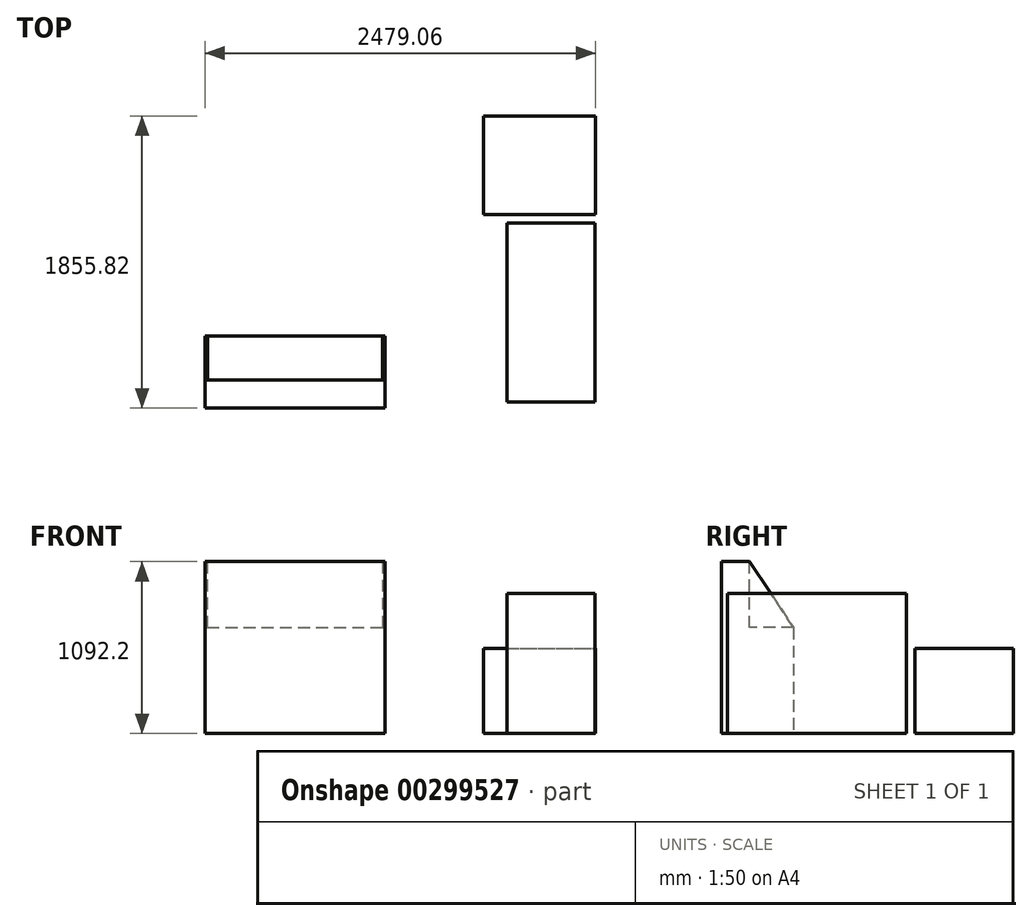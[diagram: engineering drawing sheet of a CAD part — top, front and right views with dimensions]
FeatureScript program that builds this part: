
annotation { "Feature Type Name" : "Feature", "Feature Type Description" : "" }
export const myFeature = defineFeature(function(context is Context, id is Id, definition is map)
    precondition{}
    {
        {
            var Q0;
            Q0=qCreatedBy(makeId("Top.planeOp"),FACE);
            var sketch = newSketch(context, id + "F0", { "sketchPlane" : qUnion([Q0])});
            skLineSegment(sketch, "E0.bottom", {"start": v(0, 2438.4) * mm, "end": v(2514.6, 2438.4) * mm});
            skLineSegment(sketch, "E0.top", {"start": v(0, 0) * mm, "end": v(2514.6, 0) * mm});
            skLineSegment(sketch, "E0.right", {"start": v(2514.6, 2438.4) * mm, "end": v(2514.6, 0) * mm});
            skLineSegment(sketch, "E1", {"start": v(1117, 67) * mm, "end": v(1117, -133) * mm});
            skLineSegment(sketch, "E2", {"start": v(1879.6, 100) * mm, "end": v(1879.6, -100) * mm});
            skLineSegment(sketch, "E3.bottom", {"start": v(1930.9, 1181.51) * mm, "end": v(2489.7, 1181.51) * mm});
            skLineSegment(sketch, "E3.top", {"start": v(1930.9, 46.8) * mm, "end": v(2489.7, 46.8) * mm});
            skLineSegment(sketch, "E3.left", {"start": v(1930.9, 1181.51) * mm, "end": v(1930.9, 46.8) * mm});
            skLineSegment(sketch, "E3.right", {"start": v(2489.7, 1181.51) * mm, "end": v(2489.7, 46.8) * mm});
            skLineSegment(sketch, "E4.bottom", {"start": v(12.86, 7.01) * mm, "end": v(12.86, 464.21) * mm});
            skLineSegment(sketch, "E4.top", {"start": v(1155.86, 7.01) * mm, "end": v(1155.86, 464.21) * mm});
            skLineSegment(sketch, "E4.left", {"start": v(12.86, 7.01) * mm, "end": v(1155.86, 7.01) * mm});
            skLineSegment(sketch, "E4.right", {"start": v(12.86, 464.21) * mm, "end": v(1155.86, 464.21) * mm});
            skLineSegment(sketch, "E5.bottom", {"start": v(1674.3, 2424) * mm, "end": v(1674.3, 1894) * mm});
            skLineSegment(sketch, "E5.top", {"start": v(583.3, 2609.96) * mm, "end": v(53.3, 2609.96) * mm});
            skLineSegment(sketch, "E5.left", {"start": v(1674.3, 2424) * mm, "end": v(24.3, 2424) * mm});
            skLineSegment(sketch, "E5.right", {"start": v(1674.3, 1894) * mm, "end": v(24.3, 1894) * mm});
            skLineSegment(sketch, "E6.bottom", {"start": v(230.69, 2329.27) * mm, "end": v(1480.69, 2329.27) * mm});
            skLineSegment(sketch, "E6.top", {"start": v(230.69, 1999.27) * mm, "end": v(1480.69, 1999.27) * mm});
            skLineSegment(sketch, "E6.left", {"start": v(230.69, 2329.27) * mm, "end": v(230.69, 1999.27) * mm});
            skLineSegment(sketch, "E6.right", {"start": v(1480.69, 2329.27) * mm, "end": v(1480.69, 1999.27) * mm});
            skLineSegment(sketch, "E7.bottom", {"start": v(1781.92, 1862.83) * mm, "end": v(2491.92, 1862.83) * mm});
            skLineSegment(sketch, "E7.top", {"start": v(1781.92, 1237.83) * mm, "end": v(2491.92, 1237.83) * mm});
            skLineSegment(sketch, "E7.left", {"start": v(1781.92, 1862.83) * mm, "end": v(1781.92, 1237.83) * mm});
            skLineSegment(sketch, "E7.right", {"start": v(2491.92, 1862.83) * mm, "end": v(2491.92, 1237.83) * mm});
            skLineSegment(sketch, "E8", {"start": v(24.3, 1894) * mm, "end": v(24.3, 2424) * mm});
            skSolve(sketch);
        }
        {
            var Q0;
            Q0=makeQuery(id+"F0.imprint","IMPRINT",FACE,{"disambiguationData":[TD([[makeQuery(id+"F0.imprint","IMPRINT",EDGE,{"derivedFrom":sQuery(id+"F0.wireOp",EDGE,"E3.bottom")}),-1.0]])]});
            extrude(context, id + "F1", {"entities" : qUnion([Q0]), "depth" : 889 * mm});
        }
        {
            var Q0;
            {var subQ3=sQuery(id+"F0.wireOp",EDGE,"E4.bottom");Q0=makeQuery(id+"F0.imprint","IMPRINT",FACE,{"disambiguationData":[TD([[makeQuery(id+"F0.imprint","IMPRINT",EDGE,{"derivedFrom":subQ3}),-1.0]])]});}
            extrude(context, id + "F2", {"entities" : qUnion([Q0]), "depth" : 673.1 * mm});
        }
        {
            var Q0;
            Q0=makeQuery(id+"F2.opExtrude","CAP_FACE",FACE,{"disambiguationData":[OSD([sQuery(id+"F0.wireOp",EDGE,"E4.bottom"),sQuery(id+"F0.wireOp",EDGE,"E4.top"),sQuery(id+"F0.wireOp",EDGE,"E4.left"),sQuery(id+"F0.wireOp",EDGE,"E4.right")])],"isStart":false});
            var sketch = newSketch(context, id + "F3", { "sketchPlane" : qUnion([Q0])});
            skLineSegment(sketch, "E9.bottom", {"start": v(12.86, 7.01) * mm, "end": v(1155.86, 7.01) * mm});
            skLineSegment(sketch, "E9.top", {"start": v(12.86, 184.81) * mm, "end": v(1155.86, 184.81) * mm});
            skLineSegment(sketch, "E9.left", {"start": v(12.86, 7.01) * mm, "end": v(12.86, 184.81) * mm});
            skLineSegment(sketch, "E9.right", {"start": v(1155.86, 7.01) * mm, "end": v(1155.86, 184.81) * mm});
            skSolve(sketch);
        }
        {
            var Q0;
            Q0=makeQuery(id+"F3.imprint","IMPRINT",FACE,{"disambiguationData":[TD([[makeQuery(id+"F3.imprint","IMPRINT",EDGE,{"derivedFrom":sQuery(id+"F3.wireOp",EDGE,"E9.bottom")}),1.0]])]});
            extrude(context, id + "F4", {"entities" : qUnion([Q0]), "operationType" : NewBodyOperationType.ADD, "depth" : 419.1 * mm});
        }
        {
            var Q0;
            Q0=makeQuery(id+"F4.boolean.opBoolean","MERGE",FACE,{"derivedFrom":[makeQuery(id+"F2.opExtrude","SWEPT_FACE",FACE,{"disambiguationData":[OSD([sQuery(id+"F0.wireOp",EDGE,"E4.top")])]}),makeQuery(id+"F4.opExtrude","SWEPT_FACE",FACE,{"disambiguationData":[OSD([sQuery(id+"F3.wireOp",EDGE,"E9.right")])]})]});
            var sketch = newSketch(context, id + "F5", { "sketchPlane" : qUnion([Q0])});
            skLineSegment(sketch, "E10", {"start": v(184.81, 1092.2) * mm, "end": v(464.21, 673.1) * mm});
            skSolve(sketch);
        }
        {
            var Q0;
            {var subQ1=sQuery(id+"F0.wireOp",EDGE,"E4.top");Q0=makeQuery(id+"F5.imprint","IMPRINT",FACE,{"disambiguationData":[TD([[makeQuery(id+"F5.imprint","IMPRINT",EDGE,{"derivedFrom":makeQuery(id+"F2.opExtrude","CAP_EDGE",EDGE,{"disambiguationData":[OSD([subQ1])],"isStart":true})}),1.0]])]});}
            var Q1;
            Q1=makeQuery(id+"F5.imprint","IMPRINT",FACE,{"disambiguationData":[TD([[makeQuery(id+"F5.imprint","IMPRINT",EDGE,{"derivedFrom":sQuery(id+"F5.wireOp",EDGE,"E10")}),-1.0]])]});
            extrude(context, id + "F6", {"entities" : qUnion([Q0, Q1]), "operationType" : NewBodyOperationType.ADD, "oppositeDirection" : true, "depth" : 15 * mm});
        }
        {
            var Q0;
            Q0=makeQuery(id+"F4.boolean.opBoolean","MERGE",FACE,{"derivedFrom":[makeQuery(id+"F2.opExtrude","SWEPT_FACE",FACE,{"disambiguationData":[OSD([sQuery(id+"F0.wireOp",EDGE,"E4.bottom")])]}),makeQuery(id+"F4.opExtrude","SWEPT_FACE",FACE,{"disambiguationData":[OSD([sQuery(id+"F3.wireOp",EDGE,"E9.left")])]})]});
            var sketch = newSketch(context, id + "F7", { "sketchPlane" : qUnion([Q0])});
            skLineSegment(sketch, "E11", {"start": v(-464.21, 673.1) * mm, "end": v(-184.81, 1092.2) * mm});
            skSolve(sketch);
        }
        {
            var Q0;
            {var subQ1=sQuery(id+"F0.wireOp",EDGE,"E4.bottom");Q0=makeQuery(id+"F7.imprint","IMPRINT",FACE,{"disambiguationData":[TD([[makeQuery(id+"F7.imprint","IMPRINT",EDGE,{"derivedFrom":makeQuery(id+"F2.opExtrude","CAP_EDGE",EDGE,{"disambiguationData":[OSD([subQ1])],"isStart":true})}),-1.0]])]});}
            var Q1;
            Q1=makeQuery(id+"F7.imprint","IMPRINT",FACE,{"disambiguationData":[TD([[makeQuery(id+"F7.imprint","IMPRINT",EDGE,{"derivedFrom":sQuery(id+"F7.wireOp",EDGE,"E11")}),-1.0]])]});
            extrude(context, id + "F8", {"entities" : qUnion([Q0, Q1]), "operationType" : NewBodyOperationType.ADD, "oppositeDirection" : true, "depth" : 15 * mm});
        }
        {
            var Q0;
            Q0=makeQuery(id+"F0.imprint","IMPRINT",FACE,{"disambiguationData":[TD([[makeQuery(id+"F0.imprint","IMPRINT",EDGE,{"derivedFrom":sQuery(id+"F0.wireOp",EDGE,"E7.bottom")}),-1.0]])]});
            extrude(context, id + "F9", {"entities" : qUnion([Q0]), "depth" : 540 * mm});
        }
    });
